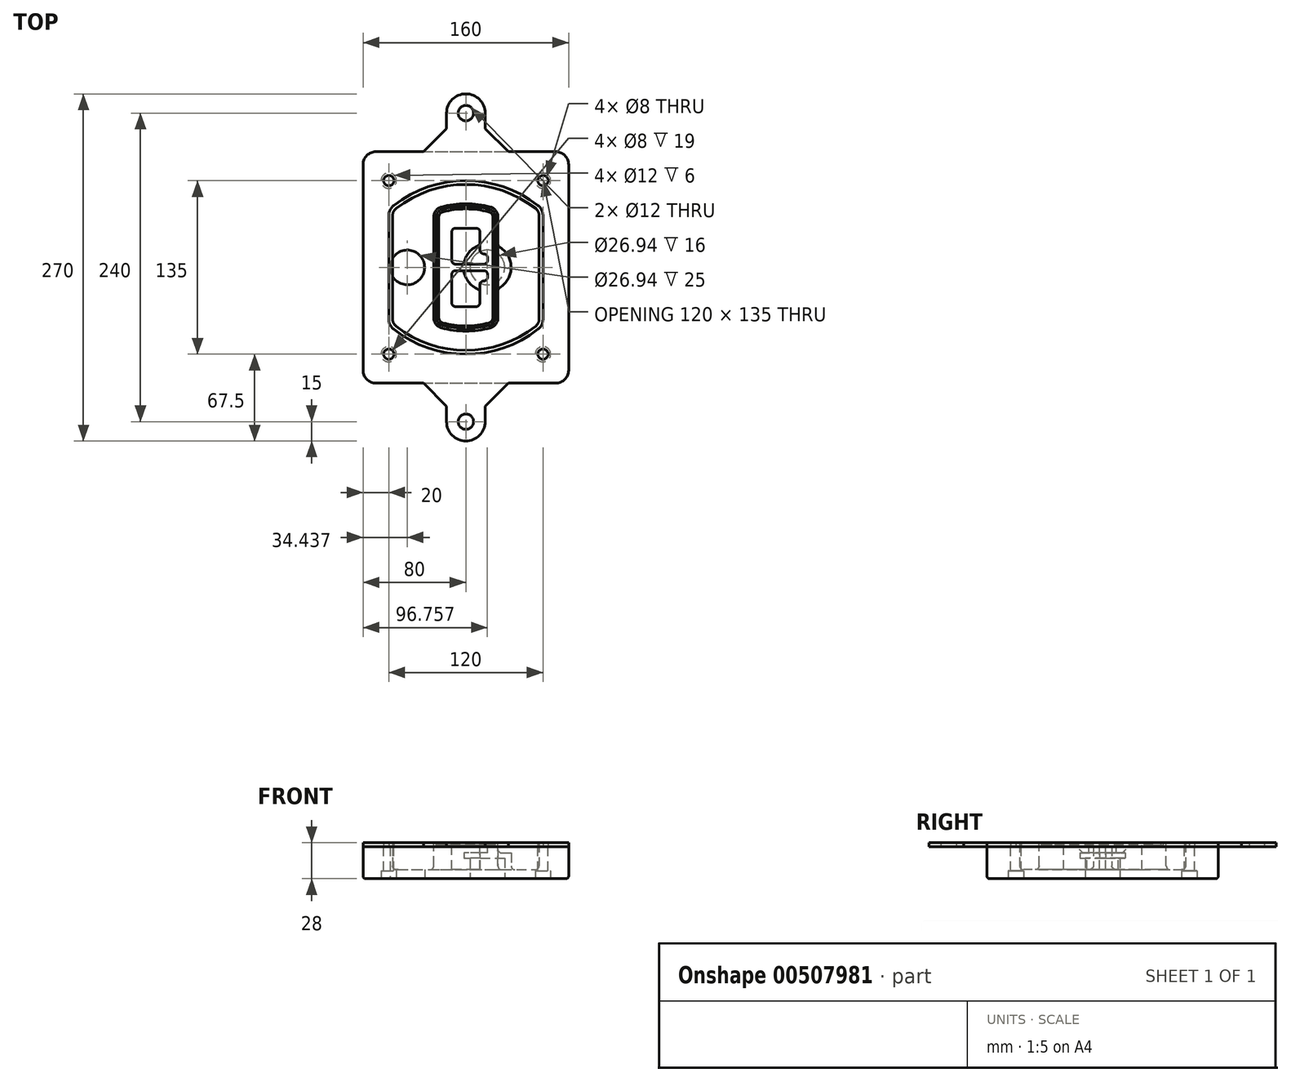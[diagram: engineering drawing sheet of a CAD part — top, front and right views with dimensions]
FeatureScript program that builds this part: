
annotation { "Feature Type Name" : "Feature", "Feature Type Description" : "" }
export const myFeature = defineFeature(function(context is Context, id is Id, definition is map)
    precondition{}
    {
        {
            var Q0;
            Q0=qCreatedBy(makeId("Top.planeOp"),FACE);
            var sketch = newSketch(context, id + "F0", { "sketchPlane" : qUnion([Q0])});
            skPoint(sketch, "E0.rect.middle", {"position": v(0, 0) * mm});
            skLineSegment(sketch, "E1.bottom", {"start": v(-70, -90) * mm, "end": v(70, -90) * mm});
            skLineSegment(sketch, "E1.top", {"start": v(-70, 90) * mm, "end": v(70, 90) * mm});
            skLineSegment(sketch, "E1.left", {"start": v(-80, -80) * mm, "end": v(-80, 80) * mm});
            skLineSegment(sketch, "E1.right", {"start": v(80, -80) * mm, "end": v(80, 80) * mm});
            skLineSegment(sketch, "E2", {"start": v(-80, 90) * mm, "end": v(80, -90) * mm, "construction": true});
            skLineSegment(sketch, "E3", {"start": v(80, 90) * mm, "end": v(-80, -90) * mm, "construction": true});
            skCircle(sketch, "E4", {"center": v(-60, 67.5) * mm, "radius": 4 * mm});
            skCircle(sketch, "E5", {"center": v(60, 67.5) * mm, "radius": 4 * mm});
            skCircle(sketch, "E6", {"center": v(60, -67.5) * mm, "radius": 4 * mm});
            skCircle(sketch, "E7", {"center": v(-60, -67.5) * mm, "radius": 4 * mm});
            skLineSegment(sketch, "E8", {"start": v(-60, 67.5) * mm, "end": v(60, 67.5) * mm, "construction": true});
            skLineSegment(sketch, "E9", {"start": v(60, 67.5) * mm, "end": v(60, -67.5) * mm, "construction": true});
            skLineSegment(sketch, "E10", {"start": v(60, -67.5) * mm, "end": v(-60, -67.5) * mm, "construction": true});
            skLineSegment(sketch, "E11", {"start": v(-60, -67.5) * mm, "end": v(-60, 67.5) * mm, "construction": true});
            skLineSegment(sketch, "E12", {"start": v(-60, 40.3) * mm, "end": v(-60, -40.3) * mm});
            skLineSegment(sketch, "E13", {"start": v(60, 40.3) * mm, "end": v(60, -40.3) * mm});
            skArc(sketch, "E14", {"start": v(56.15, 48.18) * mm, "mid": v(0, 67.5) * mm, "end": v(-56.15, 48.18) * mm});
            skArc(sketch, "E15", {"start": v(-56.15, -48.18) * mm, "mid": v(0, -67.5) * mm, "end": v(56.15, -48.18) * mm});
            skLineSegment(sketch, "E16", {"start": v(-60, 0) * mm, "end": v(60, 0) * mm, "construction": true});
            skPoint(sketch, "E17.visualSharp", {"position": v(-60, -45) * mm});
            skArc(sketch, "E17.filletArc", {"start": v(-60, -40.3) * mm, "mid": v(-58.99, -44.68) * mm, "end": v(-56.15, -48.18) * mm});
            skPoint(sketch, "E18.visualSharp", {"position": v(-60, 45) * mm});
            skArc(sketch, "E18.filletArc", {"start": v(-56.15, 48.18) * mm, "mid": v(-58.99, 44.68) * mm, "end": v(-60, 40.3) * mm});
            skPoint(sketch, "E19.visualSharp", {"position": v(60, 45) * mm});
            skArc(sketch, "E19.filletArc", {"start": v(60, 40.3) * mm, "mid": v(58.99, 44.68) * mm, "end": v(56.15, 48.18) * mm});
            skPoint(sketch, "E20.visualSharp", {"position": v(60, -45) * mm});
            skArc(sketch, "E20.filletArc", {"start": v(56.15, -48.18) * mm, "mid": v(58.99, -44.68) * mm, "end": v(60, -40.3) * mm});
            skPoint(sketch, "E21.visualSharp", {"position": v(-80, 90) * mm});
            skArc(sketch, "E21.filletArc", {"start": v(-70, 90) * mm, "mid": v(-77.07, 87.07) * mm, "end": v(-80, 80) * mm});
            skPoint(sketch, "E22.visualSharp", {"position": v(80, 90) * mm});
            skArc(sketch, "E22.filletArc", {"start": v(80, 80) * mm, "mid": v(77.07, 87.07) * mm, "end": v(70, 90) * mm});
            skPoint(sketch, "E23.visualSharp", {"position": v(80, -90) * mm});
            skArc(sketch, "E23.filletArc", {"start": v(70, -90) * mm, "mid": v(77.07, -87.07) * mm, "end": v(80, -80) * mm});
            skPoint(sketch, "E24.visualSharp", {"position": v(-80, -90) * mm});
            skArc(sketch, "E24.filletArc", {"start": v(-80, -80) * mm, "mid": v(-77.07, -87.07) * mm, "end": v(-70, -90) * mm});
            skArc(sketch, "E25.0", {"start": v(57, 40.3) * mm, "mid": v(56.3, 43.36) * mm, "end": v(54.3, 45.81) * mm});
            skLineSegment(sketch, "E25.1", {"start": v(57, 40.3) * mm, "end": v(57, -40.3) * mm});
            skArc(sketch, "E25.2", {"start": v(54.3, -45.81) * mm, "mid": v(56.3, -43.36) * mm, "end": v(57, -40.3) * mm});
            skArc(sketch, "E25.3", {"start": v(-54.3, -45.81) * mm, "mid": v(0, -64.5) * mm, "end": v(54.3, -45.81) * mm});
            skArc(sketch, "E25.4", {"start": v(-57, -40.3) * mm, "mid": v(-56.3, -43.36) * mm, "end": v(-54.3, -45.81) * mm});
            skArc(sketch, "E25.5", {"start": v(54.3, 45.81) * mm, "mid": v(0, 64.5) * mm, "end": v(-54.3, 45.81) * mm});
            skLineSegment(sketch, "E25.6", {"start": v(-57, 40.3) * mm, "end": v(-57, -40.3) * mm});
            skArc(sketch, "E25.7", {"start": v(-54.3, 45.81) * mm, "mid": v(-56.3, 43.36) * mm, "end": v(-57, 40.3) * mm});
            skArc(sketch, "E26.0", {"start": v(-58.62, 51.33) * mm, "mid": v(-62.58, 46.43) * mm, "end": v(-64, 40.3) * mm});
            skArc(sketch, "E26.1", {"start": v(58.62, 51.33) * mm, "mid": v(0, 71.5) * mm, "end": v(-58.62, 51.33) * mm});
            skArc(sketch, "E26.2", {"start": v(64, 40.3) * mm, "mid": v(62.58, 46.43) * mm, "end": v(58.62, 51.33) * mm});
            skLineSegment(sketch, "E26.3", {"start": v(64, 40.3) * mm, "end": v(64, -40.3) * mm});
            skArc(sketch, "E26.4", {"start": v(58.62, -51.33) * mm, "mid": v(62.58, -46.43) * mm, "end": v(64, -40.3) * mm});
            skLineSegment(sketch, "E26.5", {"start": v(-64, 40.3) * mm, "end": v(-64, -40.3) * mm});
            skArc(sketch, "E26.6", {"start": v(-58.62, -51.33) * mm, "mid": v(0, -71.5) * mm, "end": v(58.62, -51.33) * mm});
            skArc(sketch, "E26.7", {"start": v(-64, -40.3) * mm, "mid": v(-62.58, -46.43) * mm, "end": v(-58.62, -51.33) * mm});
            skSolve(sketch);
        }
        {
            var Q0;
            Q0=makeQuery(id+"F0.imprint","IMPRINT",FACE,{"disambiguationData":[TD([[makeQuery(id+"F0.imprint","IMPRINT",EDGE,{"derivedFrom":sQuery(id+"F0.wireOp",EDGE,"E1.bottom")}),1.0]])]});
            var Q1;
            Q1=makeQuery(id+"F0.imprint","IMPRINT",FACE,{"disambiguationData":[TD([[makeQuery(id+"F0.imprint","IMPRINT",EDGE,{"derivedFrom":sQuery(id+"F0.wireOp",EDGE,"E12")}),1.0]])]});
            var Q2;
            Q2=makeQuery(id+"F0.imprint","IMPRINT",FACE,{"disambiguationData":[TD([[makeQuery(id+"F0.imprint","IMPRINT",EDGE,{"derivedFrom":sQuery(id+"F0.wireOp",EDGE,"E25.0")}),1.0]])]});
            var Q3;
            Q3=makeQuery(id+"F0.imprint","IMPRINT",FACE,{"disambiguationData":[TD([[makeQuery(id+"F0.imprint","IMPRINT",EDGE,{"derivedFrom":sQuery(id+"F0.wireOp",EDGE,"E12")}),-1.0]])]});
            extrude(context, id + "F1", {"entities" : qUnion([Q0, Q1, Q2, Q3]), "oppositeDirection" : true, "depth" : 25 * mm});
        }
        {
            var Q0;
            Q0=makeQuery(id+"F0.imprint","IMPRINT",FACE,{"disambiguationData":[TD([[makeQuery(id+"F0.imprint","IMPRINT",EDGE,{"derivedFrom":sQuery(id+"F0.wireOp",EDGE,"E12")}),1.0]])]});
            extrude(context, id + "F2", {"entities" : qUnion([Q0]), "operationType" : NewBodyOperationType.ADD, "depth" : 3 * mm});
        }
        {
            var Q0;
            Q0=makeQuery(id+"F0.imprint","IMPRINT",FACE,{"disambiguationData":[TD([[makeQuery(id+"F0.imprint","IMPRINT",EDGE,{"derivedFrom":sQuery(id+"F0.wireOp",EDGE,"E25.0")}),1.0]])]});
            extrude(context, id + "F3", {"entities" : qUnion([Q0]), "operationType" : NewBodyOperationType.REMOVE, "oppositeDirection" : true, "depth" : 18 * mm});
        }
        {
            var Q0;
            Q0=makeQuery(id+"F2.opExtrude","CAP_FACE",FACE,{"disambiguationData":[OSD([sQuery(id+"F0.wireOp",EDGE,"E12"),sQuery(id+"F0.wireOp",EDGE,"E13"),sQuery(id+"F0.wireOp",EDGE,"E14"),sQuery(id+"F0.wireOp",EDGE,"E15"),sQuery(id+"F0.wireOp",EDGE,"E17.filletArc"),sQuery(id+"F0.wireOp",EDGE,"E18.filletArc"),sQuery(id+"F0.wireOp",EDGE,"E19.filletArc"),sQuery(id+"F0.wireOp",EDGE,"E20.filletArc"),sQuery(id+"F0.wireOp",EDGE,"E25.0"),sQuery(id+"F0.wireOp",EDGE,"E25.1"),sQuery(id+"F0.wireOp",EDGE,"E25.2"),sQuery(id+"F0.wireOp",EDGE,"E25.3"),sQuery(id+"F0.wireOp",EDGE,"E25.4"),sQuery(id+"F0.wireOp",EDGE,"E25.5"),sQuery(id+"F0.wireOp",EDGE,"E25.6"),sQuery(id+"F0.wireOp",EDGE,"E25.7")])],"isStart":false});
            var sketch = newSketch(context, id + "F4", { "sketchPlane" : qUnion([Q0])});
            skArc(sketch, "E27.0", {"start": v(-19.08, -46.97) * mm, "mid": v(0, -49.5) * mm, "end": v(19.08, -46.97) * mm});
            skArc(sketch, "E28.0", {"start": v(19.08, 46.97) * mm, "mid": v(0, 49.5) * mm, "end": v(-19.08, 46.97) * mm});
            skLineSegment(sketch, "E29", {"start": v(-25, 39.25) * mm, "end": v(-25, -39.25) * mm});
            skLineSegment(sketch, "E30", {"start": v(25, 39.25) * mm, "end": v(25, -39.25) * mm});
            skLineSegment(sketch, "E31", {"start": v(-25, 45.1) * mm, "end": v(25, 45.1) * mm, "construction": true});
            skLineSegment(sketch, "E32", {"start": v(-25, -45.1) * mm, "end": v(25, -45.1) * mm, "construction": true});
            skPoint(sketch, "E33.visualSharp", {"position": v(-25, 45.1) * mm});
            skArc(sketch, "E33.filletArc", {"start": v(-19.08, 46.97) * mm, "mid": v(-23.35, 44.11) * mm, "end": v(-25, 39.25) * mm});
            skPoint(sketch, "E34.visualSharp", {"position": v(25, 45.1) * mm});
            skArc(sketch, "E34.filletArc", {"start": v(25, 39.25) * mm, "mid": v(23.35, 44.11) * mm, "end": v(19.08, 46.97) * mm});
            skPoint(sketch, "E35.visualSharp", {"position": v(25, -45.1) * mm});
            skArc(sketch, "E35.filletArc", {"start": v(19.08, -46.97) * mm, "mid": v(23.35, -44.11) * mm, "end": v(25, -39.25) * mm});
            skPoint(sketch, "E36.visualSharp", {"position": v(-25, -45.1) * mm});
            skArc(sketch, "E36.filletArc", {"start": v(-25, -39.25) * mm, "mid": v(-23.35, -44.11) * mm, "end": v(-19.08, -46.97) * mm});
            skArc(sketch, "E37.0", {"start": v(54.3, 45.81) * mm, "mid": v(0, 64.5) * mm, "end": v(-54.3, 45.81) * mm});
            skArc(sketch, "E37.1", {"start": v(-54.3, 45.81) * mm, "mid": v(-56.3, 43.36) * mm, "end": v(-57, 40.3) * mm});
            skLineSegment(sketch, "E37.2", {"start": v(-57, 40.3) * mm, "end": v(-57, -40.3) * mm});
            skArc(sketch, "E37.3", {"start": v(-57, -40.3) * mm, "mid": v(-56.3, -43.36) * mm, "end": v(-54.3, -45.81) * mm});
            skArc(sketch, "E37.4", {"start": v(-54.3, -45.81) * mm, "mid": v(0, -64.5) * mm, "end": v(54.3, -45.81) * mm});
            skArc(sketch, "E37.5", {"start": v(54.3, -45.81) * mm, "mid": v(56.3, -43.36) * mm, "end": v(57, -40.3) * mm});
            skLineSegment(sketch, "E37.6", {"start": v(57, 40.3) * mm, "end": v(57, -40.3) * mm});
            skArc(sketch, "E37.7", {"start": v(57, 40.3) * mm, "mid": v(56.3, 43.36) * mm, "end": v(54.3, 45.81) * mm});
            skLineSegment(sketch, "E38.0", {"start": v(23, 39.25) * mm, "end": v(23, -39.25) * mm});
            skArc(sketch, "E38.1", {"start": v(18.56, -45.04) * mm, "mid": v(21.76, -42.9) * mm, "end": v(23, -39.25) * mm});
            skArc(sketch, "E38.2", {"start": v(-18.56, -45.04) * mm, "mid": v(0, -47.5) * mm, "end": v(18.56, -45.04) * mm});
            skArc(sketch, "E38.3", {"start": v(-23, -39.25) * mm, "mid": v(-21.76, -42.9) * mm, "end": v(-18.56, -45.04) * mm});
            skLineSegment(sketch, "E38.4", {"start": v(-23, 39.25) * mm, "end": v(-23, -39.25) * mm});
            skArc(sketch, "E38.5", {"start": v(23, 39.25) * mm, "mid": v(21.76, 42.9) * mm, "end": v(18.56, 45.04) * mm});
            skArc(sketch, "E38.6", {"start": v(-18.56, 45.04) * mm, "mid": v(-21.76, 42.9) * mm, "end": v(-23, 39.25) * mm});
            skArc(sketch, "E38.7", {"start": v(18.56, 45.04) * mm, "mid": v(0, 47.5) * mm, "end": v(-18.56, 45.04) * mm});
            skArc(sketch, "E39.0", {"start": v(21, 39.25) * mm, "mid": v(20.18, 41.68) * mm, "end": v(18.04, 43.1) * mm});
            skLineSegment(sketch, "E39.1", {"start": v(21, 39.25) * mm, "end": v(21, -39.25) * mm});
            skArc(sketch, "E39.2", {"start": v(18.04, -43.1) * mm, "mid": v(20.18, -41.68) * mm, "end": v(21, -39.25) * mm});
            skArc(sketch, "E39.3", {"start": v(-18.04, -43.1) * mm, "mid": v(0, -45.5) * mm, "end": v(18.04, -43.1) * mm});
            skArc(sketch, "E39.4", {"start": v(-21, -39.25) * mm, "mid": v(-20.18, -41.68) * mm, "end": v(-18.04, -43.1) * mm});
            skArc(sketch, "E39.5", {"start": v(18.04, 43.1) * mm, "mid": v(0, 45.5) * mm, "end": v(-18.04, 43.1) * mm});
            skLineSegment(sketch, "E39.6", {"start": v(-21, 39.25) * mm, "end": v(-21, -39.25) * mm});
            skArc(sketch, "E39.7", {"start": v(-18.04, 43.1) * mm, "mid": v(-20.18, 41.68) * mm, "end": v(-21, 39.25) * mm});
            skLineSegment(sketch, "E40", {"start": v(-25, 0) * mm, "end": v(25, 0) * mm, "construction": true});
            skLineSegment(sketch, "E41", {"start": v(-11, 5.5) * mm, "end": v(-11, 27.5) * mm});
            skLineSegment(sketch, "E42", {"start": v(-8, 30.5) * mm, "end": v(8, 30.5) * mm});
            skLineSegment(sketch, "E43", {"start": v(11, 27.5) * mm, "end": v(11, 13.5) * mm});
            skLineSegment(sketch, "E44", {"start": v(14, 10.5) * mm, "end": v(14, 10.5) * mm});
            skLineSegment(sketch, "E45", {"start": v(17, 7.5) * mm, "end": v(17, 5.5) * mm});
            skLineSegment(sketch, "E46", {"start": v(14, 2.5) * mm, "end": v(-8, 2.5) * mm});
            skPoint(sketch, "E47.visualSharp", {"position": v(-11, 30.5) * mm});
            skArc(sketch, "E47.filletArc", {"start": v(-8, 30.5) * mm, "mid": v(-10.12, 29.62) * mm, "end": v(-11, 27.5) * mm});
            skPoint(sketch, "E48.visualSharp", {"position": v(11, 30.5) * mm});
            skArc(sketch, "E48.filletArc", {"start": v(11, 27.5) * mm, "mid": v(10.12, 29.62) * mm, "end": v(8, 30.5) * mm});
            skPoint(sketch, "E49.visualSharp", {"position": v(11, 10.5) * mm});
            skArc(sketch, "E49.filletArc", {"start": v(11, 13.5) * mm, "mid": v(11.88, 11.38) * mm, "end": v(14, 10.5) * mm});
            skPoint(sketch, "E50.visualSharp", {"position": v(17, 10.5) * mm});
            skArc(sketch, "E50.filletArc", {"start": v(17, 7.5) * mm, "mid": v(16.12, 9.62) * mm, "end": v(14, 10.5) * mm});
            skPoint(sketch, "E51.visualSharp", {"position": v(17, 2.5) * mm});
            skArc(sketch, "E51.filletArc", {"start": v(14, 2.5) * mm, "mid": v(16.12, 3.38) * mm, "end": v(17, 5.5) * mm});
            skPoint(sketch, "E52.visualSharp", {"position": v(-11, 2.5) * mm});
            skArc(sketch, "E52.filletArc", {"start": v(-11, 5.5) * mm, "mid": v(-10.12, 3.38) * mm, "end": v(-8, 2.5) * mm});
            skLineSegment(sketch, "E53.0.MirrorCS", {"start": v(14, -2.5) * mm, "end": v(-8, -2.5) * mm});
            skArc(sketch, "E54.0.MirrorCS", {"start": v(-11, -5.5) * mm, "mid": v(-10.12, -3.38) * mm, "end": v(-8, -2.5) * mm});
            skLineSegment(sketch, "E55.0.MirrorCS", {"start": v(-11, -5.5) * mm, "end": v(-11, -27.5) * mm});
            skArc(sketch, "E56.0.MirrorCS", {"start": v(-8, -30.5) * mm, "mid": v(-10.12, -29.62) * mm, "end": v(-11, -27.5) * mm});
            skLineSegment(sketch, "E57.0.MirrorCS", {"start": v(-8, -30.5) * mm, "end": v(8, -30.5) * mm});
            skArc(sketch, "E58.0.MirrorCS", {"start": v(11, -27.5) * mm, "mid": v(10.12, -29.62) * mm, "end": v(8, -30.5) * mm});
            skLineSegment(sketch, "E59.0.MirrorCS", {"start": v(11, -27.5) * mm, "end": v(11, -13.5) * mm});
            skArc(sketch, "E60.0.MirrorCS", {"start": v(11, -13.5) * mm, "mid": v(11.88, -11.38) * mm, "end": v(14, -10.5) * mm});
            skArc(sketch, "E61.0.MirrorCS", {"start": v(17, -7.5) * mm, "mid": v(16.12, -9.62) * mm, "end": v(14, -10.5) * mm});
            skLineSegment(sketch, "E62.0.MirrorCS", {"start": v(17, -7.5) * mm, "end": v(17, -5.5) * mm});
            skArc(sketch, "E63.0.MirrorCS", {"start": v(14, -2.5) * mm, "mid": v(16.12, -3.38) * mm, "end": v(17, -5.5) * mm});
            skSolve(sketch);
        }
        {
            var Q0;
            Q0=makeQuery(id+"F4.imprint","IMPRINT",FACE,{"disambiguationData":[TD([[makeQuery(id+"F4.imprint","IMPRINT",EDGE,{"derivedFrom":sQuery(id+"F4.wireOp",EDGE,"E27.0")}),1.0]])]});
            var Q1;
            Q1=makeQuery(id+"F4.imprint","IMPRINT",FACE,{"disambiguationData":[TD([[makeQuery(id+"F4.imprint","IMPRINT",EDGE,{"derivedFrom":sQuery(id+"F4.wireOp",EDGE,"E38.0")}),-1.0]])]});
            var Q2;
            Q2=makeQuery(id+"F4.imprint","IMPRINT",FACE,{"disambiguationData":[TD([[makeQuery(id+"F4.imprint","IMPRINT",EDGE,{"derivedFrom":sQuery(id+"F4.wireOp",EDGE,"E39.0")}),1.0]])]});
            extrude(context, id + "F5", {"entities" : qUnion([Q0, Q1, Q2]), "operationType" : NewBodyOperationType.ADD, "endBound" : BoundingType.UP_TO_NEXT, "oppositeDirection" : true, "depth" : 25 * mm});
        }
        {
            var Q0;
            Q0=makeQuery(id+"F4.imprint","IMPRINT",FACE,{"disambiguationData":[TD([[makeQuery(id+"F4.imprint","IMPRINT",EDGE,{"derivedFrom":sQuery(id+"F4.wireOp",EDGE,"E38.0")}),-1.0]])]});
            extrude(context, id + "F6", {"entities" : qUnion([Q0]), "operationType" : NewBodyOperationType.REMOVE, "oppositeDirection" : true, "depth" : 2 * mm});
        }
        {
            var Q0;
            Q0=makeQuery(id+"F1.opExtrude","CAP_FACE",FACE,{"disambiguationData":[OSD([sQuery(id+"F0.wireOp",EDGE,"E1.bottom"),sQuery(id+"F0.wireOp",EDGE,"E1.top"),sQuery(id+"F0.wireOp",EDGE,"E1.left"),sQuery(id+"F0.wireOp",EDGE,"E1.right"),sQuery(id+"F0.wireOp",EDGE,"E4"),sQuery(id+"F0.wireOp",EDGE,"E5"),sQuery(id+"F0.wireOp",EDGE,"E6"),sQuery(id+"F0.wireOp",EDGE,"E7"),sQuery(id+"F0.wireOp",EDGE,"E21.filletArc"),sQuery(id+"F0.wireOp",EDGE,"E22.filletArc"),sQuery(id+"F0.wireOp",EDGE,"E23.filletArc"),sQuery(id+"F0.wireOp",EDGE,"E24.filletArc")])],"isStart":false});
            var sketch = newSketch(context, id + "F7", { "sketchPlane" : qUnion([Q0])});
            skCircle(sketch, "E64", {"center": v(16.76, 0) * mm, "radius": 13.47 * mm});
            skCircle(sketch, "E65", {"center": v(-45.56, 0) * mm, "radius": 13.47 * mm});
            skLineSegment(sketch, "E66", {"start": v(80, 0) * mm, "end": v(-80, 0) * mm});
            skCircle(sketch, "E67", {"center": v(16.76, 0) * mm, "radius": 18.47 * mm});
            skCircle(sketch, "E68", {"center": v(60, -67.5) * mm, "radius": 6 * mm});
            skCircle(sketch, "E69", {"center": v(-60, -67.5) * mm, "radius": 6 * mm});
            skCircle(sketch, "E70", {"center": v(-60, 67.5) * mm, "radius": 6 * mm});
            skCircle(sketch, "E71", {"center": v(60, 67.5) * mm, "radius": 6 * mm});
            skSolve(sketch);
        }
        {
            var Q0;
            {var subQ1=sQuery(id+"F7.wireOp",EDGE,"E66");var subQ4=sQuery(id+"F7.wireOp",EDGE,"E64");var subQ6=makeQuery(id+"F7.imprint","INTERSECT",VERTEX,{"disambiguationData":[OD(0.0)],"derivedFrom":[subQ4,subQ1]});Q0=makeQuery(id+"F7.imprint","IMPRINT",FACE,{"disambiguationData":[TD([[makeQuery(id+"F7.imprint","IMPRINT",EDGE,{"disambiguationData":[TD([[subQ6,-1.0]])],"derivedFrom":subQ4}),-1.0]])]});}
            var Q1;
            {var subQ0=sQuery(id+"F7.wireOp",EDGE,"E66");var subQ1=sQuery(id+"F7.wireOp",EDGE,"E64");var subQ3=makeQuery(id+"F7.imprint","INTERSECT",VERTEX,{"disambiguationData":[OD(0.0)],"derivedFrom":[subQ1,subQ0]});Q1=makeQuery(id+"F7.imprint","IMPRINT",FACE,{"disambiguationData":[TD([[makeQuery(id+"F7.imprint","IMPRINT",EDGE,{"disambiguationData":[TD([[subQ3,-1.0]])],"derivedFrom":subQ1}),1.0]])]});}
            var Q2;
            {var subQ0=sQuery(id+"F7.wireOp",EDGE,"E66");var subQ1=sQuery(id+"F7.wireOp",EDGE,"E64");var subQ3=makeQuery(id+"F7.imprint","INTERSECT",VERTEX,{"disambiguationData":[OD(0.0)],"derivedFrom":[subQ1,subQ0]});Q2=makeQuery(id+"F7.imprint","IMPRINT",FACE,{"disambiguationData":[TD([[makeQuery(id+"F7.imprint","IMPRINT",EDGE,{"disambiguationData":[TD([[subQ3,1.0]])],"derivedFrom":subQ1}),1.0]])]});}
            var Q3;
            {var subQ1=sQuery(id+"F7.wireOp",EDGE,"E66");var subQ4=sQuery(id+"F7.wireOp",EDGE,"E64");var subQ6=makeQuery(id+"F7.imprint","INTERSECT",VERTEX,{"disambiguationData":[OD(0.0)],"derivedFrom":[subQ4,subQ1]});Q3=makeQuery(id+"F7.imprint","IMPRINT",FACE,{"disambiguationData":[TD([[makeQuery(id+"F7.imprint","IMPRINT",EDGE,{"disambiguationData":[TD([[subQ6,1.0]])],"derivedFrom":subQ4}),-1.0]])]});}
            extrude(context, id + "F8", {"entities" : qUnion([Q0, Q1, Q2, Q3]), "operationType" : NewBodyOperationType.ADD, "oppositeDirection" : true, "depth" : 20 * mm});
        }
        {
            var Q0;
            {var subQ0=sQuery(id+"F7.wireOp",EDGE,"E66");var subQ1=sQuery(id+"F7.wireOp",EDGE,"E64");var subQ3=makeQuery(id+"F7.imprint","INTERSECT",VERTEX,{"disambiguationData":[OD(0.0)],"derivedFrom":[subQ1,subQ0]});Q0=makeQuery(id+"F7.imprint","IMPRINT",FACE,{"disambiguationData":[TD([[makeQuery(id+"F7.imprint","IMPRINT",EDGE,{"disambiguationData":[TD([[subQ3,-1.0]])],"derivedFrom":subQ1}),1.0]])]});}
            var Q1;
            {var subQ0=sQuery(id+"F7.wireOp",EDGE,"E66");var subQ1=sQuery(id+"F7.wireOp",EDGE,"E64");var subQ3=makeQuery(id+"F7.imprint","INTERSECT",VERTEX,{"disambiguationData":[OD(0.0)],"derivedFrom":[subQ1,subQ0]});Q1=makeQuery(id+"F7.imprint","IMPRINT",FACE,{"disambiguationData":[TD([[makeQuery(id+"F7.imprint","IMPRINT",EDGE,{"disambiguationData":[TD([[subQ3,1.0]])],"derivedFrom":subQ1}),1.0]])]});}
            extrude(context, id + "F9", {"entities" : qUnion([Q0, Q1]), "operationType" : NewBodyOperationType.REMOVE, "oppositeDirection" : true, "depth" : 16 * mm});
        }
        {
            var Q0;
            {var subQ0=sQuery(id+"F7.wireOp",EDGE,"E66");var subQ1=sQuery(id+"F7.wireOp",EDGE,"E65");var subQ3=makeQuery(id+"F7.imprint","INTERSECT",VERTEX,{"disambiguationData":[OD(0.0)],"derivedFrom":[subQ1,subQ0]});Q0=makeQuery(id+"F7.imprint","IMPRINT",FACE,{"disambiguationData":[TD([[makeQuery(id+"F7.imprint","IMPRINT",EDGE,{"disambiguationData":[TD([[subQ3,-1.0]])],"derivedFrom":subQ1}),1.0]])]});}
            var Q1;
            {var subQ0=sQuery(id+"F7.wireOp",EDGE,"E66");var subQ1=sQuery(id+"F7.wireOp",EDGE,"E65");var subQ3=makeQuery(id+"F7.imprint","INTERSECT",VERTEX,{"disambiguationData":[OD(0.0)],"derivedFrom":[subQ1,subQ0]});Q1=makeQuery(id+"F7.imprint","IMPRINT",FACE,{"disambiguationData":[TD([[makeQuery(id+"F7.imprint","IMPRINT",EDGE,{"disambiguationData":[TD([[subQ3,1.0]])],"derivedFrom":subQ1}),1.0]])]});}
            extrude(context, id + "F10", {"entities" : qUnion([Q0, Q1]), "operationType" : NewBodyOperationType.REMOVE, "oppositeDirection" : true, "depth" : 25 * mm});
        }
        {
            var Q0;
            Q0=makeQuery(id+"F7.imprint","IMPRINT",FACE,{"disambiguationData":[TD([[makeQuery(id+"F7.imprint","IMPRINT",EDGE,{"derivedFrom":sQuery(id+"F7.wireOp",EDGE,"E68")}),1.0]])]});
            var Q1;
            Q1=makeQuery(id+"F7.imprint","IMPRINT",FACE,{"disambiguationData":[TD([[makeQuery(id+"F7.imprint","IMPRINT",EDGE,{"derivedFrom":makeQuery(id+"F1.opExtrude","CAP_EDGE",EDGE,{"disambiguationData":[OSD([sQuery(id+"F0.wireOp",EDGE,"E5")])],"isStart":false})}),-1.0]])]});
            var Q2;
            Q2=makeQuery(id+"F7.imprint","IMPRINT",FACE,{"disambiguationData":[TD([[makeQuery(id+"F7.imprint","IMPRINT",EDGE,{"derivedFrom":sQuery(id+"F7.wireOp",EDGE,"E69")}),1.0]])]});
            var Q3;
            Q3=makeQuery(id+"F7.imprint","IMPRINT",FACE,{"disambiguationData":[TD([[makeQuery(id+"F7.imprint","IMPRINT",EDGE,{"derivedFrom":makeQuery(id+"F1.opExtrude","CAP_EDGE",EDGE,{"disambiguationData":[OSD([sQuery(id+"F0.wireOp",EDGE,"E4")])],"isStart":false})}),-1.0]])]});
            var Q4;
            Q4=makeQuery(id+"F7.imprint","IMPRINT",FACE,{"disambiguationData":[TD([[makeQuery(id+"F7.imprint","IMPRINT",EDGE,{"derivedFrom":sQuery(id+"F7.wireOp",EDGE,"E70")}),1.0]])]});
            var Q5;
            Q5=makeQuery(id+"F7.imprint","IMPRINT",FACE,{"disambiguationData":[TD([[makeQuery(id+"F7.imprint","IMPRINT",EDGE,{"derivedFrom":makeQuery(id+"F1.opExtrude","CAP_EDGE",EDGE,{"disambiguationData":[OSD([sQuery(id+"F0.wireOp",EDGE,"E7")])],"isStart":false})}),-1.0]])]});
            var Q6;
            Q6=makeQuery(id+"F7.imprint","IMPRINT",FACE,{"disambiguationData":[TD([[makeQuery(id+"F7.imprint","IMPRINT",EDGE,{"derivedFrom":sQuery(id+"F7.wireOp",EDGE,"E71")}),1.0]])]});
            var Q7;
            Q7=makeQuery(id+"F7.imprint","IMPRINT",FACE,{"disambiguationData":[TD([[makeQuery(id+"F7.imprint","IMPRINT",EDGE,{"derivedFrom":makeQuery(id+"F1.opExtrude","CAP_EDGE",EDGE,{"disambiguationData":[OSD([sQuery(id+"F0.wireOp",EDGE,"E6")])],"isStart":false})}),-1.0]])]});
            extrude(context, id + "F11", {"entities" : qUnion([Q0, Q1, Q2, Q3, Q4, Q5, Q6, Q7]), "operationType" : NewBodyOperationType.REMOVE, "oppositeDirection" : true, "depth" : 6 * mm});
        }
        {
            var Q0;
            Q0=makeQuery(id+"F9.boolean.opBoolean","COPY",FACE,{"derivedFrom":makeQuery(id+"F9.opExtrude","CAP_FACE",FACE,{"disambiguationData":[OSD([sQuery(id+"F7.wireOp",EDGE,"E64")])],"isStart":false})});
            var sketch = newSketch(context, id + "F12", { "sketchPlane" : qUnion([Q0])});
            skArc(sketch, "E72.0", {"start": v(11, 17.55) * mm, "mid": v(2.57, 11.82) * mm, "end": v(-1.54, 2.5) * mm});
            skArc(sketch, "E72.1", {"start": v(-1.54, -2.5) * mm, "mid": v(2.57, -11.82) * mm, "end": v(11, -17.55) * mm});
            skLineSegment(sketch, "E73", {"start": v(-1.54, -2.5) * mm, "end": v(14, -2.5) * mm});
            skLineSegment(sketch, "E74.0", {"start": v(14, 2.5) * mm, "end": v(-1.54, 2.5) * mm});
            skArc(sketch, "E74.1", {"start": v(14, 2.5) * mm, "mid": v(16.12, 3.38) * mm, "end": v(17, 5.5) * mm});
            skLineSegment(sketch, "E74.2", {"start": v(17, 7.5) * mm, "end": v(17, 5.5) * mm});
            skArc(sketch, "E74.3", {"start": v(17, 7.5) * mm, "mid": v(16.12, 9.62) * mm, "end": v(14, 10.5) * mm});
            skArc(sketch, "E74.4", {"start": v(11, 13.5) * mm, "mid": v(11.88, 11.38) * mm, "end": v(14, 10.5) * mm});
            skLineSegment(sketch, "E74.5", {"start": v(11, 17.55) * mm, "end": v(11, 13.5) * mm});
            skLineSegment(sketch, "E74.7", {"start": v(14, -2.5) * mm, "end": v(-1.54, -2.5) * mm});
            skArc(sketch, "E74.8", {"start": v(14, -2.5) * mm, "mid": v(16.12, -3.38) * mm, "end": v(17, -5.5) * mm});
            skLineSegment(sketch, "E74.9", {"start": v(17, -7.5) * mm, "end": v(17, -5.5) * mm});
            skArc(sketch, "E74.10", {"start": v(17, -7.5) * mm, "mid": v(16.12, -9.62) * mm, "end": v(14, -10.5) * mm});
            skArc(sketch, "E74.11", {"start": v(11, -13.5) * mm, "mid": v(11.88, -11.38) * mm, "end": v(14, -10.5) * mm});
            skLineSegment(sketch, "E74.12", {"start": v(11, -17.55) * mm, "end": v(11, -13.5) * mm});
            skPoint(sketch, "E75.orphan", {"position": v(11, -27.5) * mm});
            skPoint(sketch, "E76.orphan", {"position": v(-8, -2.5) * mm});
            skPoint(sketch, "E77.orphan", {"position": v(-8, 2.5) * mm});
            skPoint(sketch, "E78.orphan", {"position": v(11, 27.5) * mm});
            skSolve(sketch);
        }
        {
            var Q0;
            {var subQ7=sQuery(id+"F12.wireOp",EDGE,"E72.0");var subQ14=sQuery(id+"F12.wireOp",EDGE,"E72.1");var subQ16=sQuery(id+"F12.wireOp",EDGE,"E74.1");var subQ18=sQuery(id+"F12.wireOp",EDGE,"E74.8");Q0=qUnion([makeQuery(id+"F12.imprint","IMPRINT",FACE,{"disambiguationData":[TD([[makeQuery(id+"F12.imprint","IMPRINT",EDGE,{"derivedFrom":subQ7}),1.0]])]}),makeQuery(id+"F12.imprint","IMPRINT",FACE,{"disambiguationData":[TD([[makeQuery(id+"F12.imprint","IMPRINT",EDGE,{"derivedFrom":subQ14}),1.0]])]}),makeQuery(id+"F12.imprint","IMPRINT",FACE,{"disambiguationData":[TD([[makeQuery(id+"F12.imprint","IMPRINT",EDGE,{"derivedFrom":subQ16}),1.0]])]}),makeQuery(id+"F12.imprint","IMPRINT",FACE,{"disambiguationData":[TD([[makeQuery(id+"F12.imprint","IMPRINT",EDGE,{"derivedFrom":subQ18}),-1.0]])]})]);}
            var Q1;
            Q1=makeQuery(id+"F5.boolean.opBoolean","SPLIT",FACE,{"disambiguationData":[TD([makeQuery(id+"F5.opExtrude","SWEPT_FACE",FACE,{"disambiguationData":[OSD([sQuery(id+"F4.wireOp",EDGE,"E41")])]})])],"derivedFrom":makeQuery(id+"F3.boolean.opBoolean","COPY",FACE,{"derivedFrom":makeQuery(id+"F3.opExtrude","CAP_FACE",FACE,{"disambiguationData":[OSD([sQuery(id+"F0.wireOp",EDGE,"E25.0"),sQuery(id+"F0.wireOp",EDGE,"E25.1"),sQuery(id+"F0.wireOp",EDGE,"E25.2"),sQuery(id+"F0.wireOp",EDGE,"E25.3"),sQuery(id+"F0.wireOp",EDGE,"E25.4"),sQuery(id+"F0.wireOp",EDGE,"E25.5"),sQuery(id+"F0.wireOp",EDGE,"E25.6"),sQuery(id+"F0.wireOp",EDGE,"E25.7")])],"isStart":false})})});
            extrude(context, id + "F13", {"entities" : qUnion([Q0]), "operationType" : NewBodyOperationType.REMOVE, "endBound" : BoundingType.UP_TO_SURFACE, "endBoundEntityFace" : qUnion([Q1]), "depth" : 25 * mm});
        }
        {
            var Q0;
            Q0=makeQuery(id+"F3.boolean.opBoolean","COPY",EDGE,{"derivedFrom":makeQuery(id+"F3.opExtrude","CAP_EDGE",EDGE,{"disambiguationData":[OSD([sQuery(id+"F0.wireOp",EDGE,"E25.6")])],"isStart":false})});
            var Q1;
            Q1=makeQuery(id+"F8.boolean.opBoolean","INTERSECT",EDGE,{"derivedFrom":[makeQuery(id+"F5.opExtrude","SWEPT_FACE",FACE,{"disambiguationData":[OSD([sQuery(id+"F4.wireOp",EDGE,"E30")])]}),makeQuery(id+"F8.opExtrude","CAP_FACE",FACE,{"disambiguationData":[OSD([sQuery(id+"F7.wireOp",EDGE,"E67")])],"isStart":false})]});
            var Q2;
            Q2=makeQuery(id+"F8.boolean.opBoolean","INTERSECT",EDGE,{"disambiguationData":[OD(1.0)],"derivedFrom":[makeQuery(id+"F5.opExtrude","SWEPT_FACE",FACE,{"disambiguationData":[OSD([sQuery(id+"F4.wireOp",EDGE,"E30")])]}),makeQuery(id+"F8.opExtrude","SWEPT_FACE",FACE,{"disambiguationData":[OSD([sQuery(id+"F7.wireOp",EDGE,"E67")])]})]});
            var Q3;
            {var subQ0=sQuery(id+"F4.wireOp",EDGE,"E30");Q3=makeQuery(id+"F8.boolean.opBoolean","SPLIT",EDGE,{"disambiguationData":[TD([makeQuery(id+"F5.opExtrude","SWEPT_FACE",FACE,{"disambiguationData":[OSD([sQuery(id+"F4.wireOp",EDGE,"E35.filletArc")])]})])],"derivedFrom":makeQuery(id+"F5.opExtrude","CAP_EDGE",EDGE,{"disambiguationData":[OSD([subQ0])],"isStart":false})});}
            var Q4;
            {var subQ0=sQuery(id+"F0.wireOp",EDGE,"E25.7");var subQ1=sQuery(id+"F0.wireOp",EDGE,"E25.1");var subQ2=sQuery(id+"F0.wireOp",EDGE,"E25.6");var subQ3=sQuery(id+"F0.wireOp",EDGE,"E25.5");var subQ4=sQuery(id+"F0.wireOp",EDGE,"E25.4");var subQ5=sQuery(id+"F0.wireOp",EDGE,"E25.0");var subQ6=sQuery(id+"F0.wireOp",EDGE,"E25.2");var subQ7=sQuery(id+"F0.wireOp",EDGE,"E25.3");Q4=makeQuery(id+"F8.boolean.opBoolean","INTERSECT",EDGE,{"derivedFrom":[makeQuery(id+"F5.boolean.opBoolean","SPLIT",FACE,{"disambiguationData":[TD([makeQuery(id+"F2.opExtrude","SWEPT_FACE",FACE,{"disambiguationData":[OSD([subQ5])]})])],"derivedFrom":makeQuery(id+"F3.boolean.opBoolean","COPY",FACE,{"derivedFrom":makeQuery(id+"F3.opExtrude","CAP_FACE",FACE,{"disambiguationData":[OSD([subQ5,subQ1,subQ6,subQ7,subQ4,subQ3,subQ2,subQ0])],"isStart":false})})}),makeQuery(id+"F8.opExtrude","SWEPT_FACE",FACE,{"disambiguationData":[OSD([sQuery(id+"F7.wireOp",EDGE,"E67")])]})]});}
            var Q5;
            Q5=makeQuery(id+"F8.boolean.opBoolean","INTERSECT",EDGE,{"disambiguationData":[OD(0.0)],"derivedFrom":[makeQuery(id+"F5.opExtrude","SWEPT_FACE",FACE,{"disambiguationData":[OSD([sQuery(id+"F4.wireOp",EDGE,"E30")])]}),makeQuery(id+"F8.opExtrude","SWEPT_FACE",FACE,{"disambiguationData":[OSD([sQuery(id+"F7.wireOp",EDGE,"E67")])]})]});
            fillet(context, id + "F14", {"entities" : qUnion([Q0, Q1, Q2, Q3, Q4, Q5]), "radius" : 3 * mm, "tangentPropagation" : true, "allowEdgeOverflow" : false});
        }
        {
            var Q0;
            Q0=makeQuery(id+"F1.opExtrude","CAP_EDGE",EDGE,{"disambiguationData":[OSD([sQuery(id+"F0.wireOp",EDGE,"E1.bottom")])],"isStart":false});
            fillet(context, id + "F15", {"entities" : qUnion([Q0]), "radius" : 2 * mm, "tangentPropagation" : true, "allowEdgeOverflow" : false});
        }
        {
            var Q0;
            {var subQ0=sQuery(id+"F0.wireOp",EDGE,"E21.filletArc");var subQ1=sQuery(id+"F0.wireOp",EDGE,"E7");var subQ2=sQuery(id+"F0.wireOp",EDGE,"E6");var subQ3=sQuery(id+"F0.wireOp",EDGE,"E5");var subQ4=sQuery(id+"F0.wireOp",EDGE,"E4");var subQ5=sQuery(id+"F0.wireOp",EDGE,"E22.filletArc");var subQ6=sQuery(id+"F0.wireOp",EDGE,"E1.bottom");var subQ7=sQuery(id+"F0.wireOp",EDGE,"E1.right");var subQ8=sQuery(id+"F0.wireOp",EDGE,"E1.top");var subQ9=sQuery(id+"F0.wireOp",EDGE,"E1.left");var subQ10=sQuery(id+"F0.wireOp",EDGE,"E23.filletArc");var subQ11=sQuery(id+"F0.wireOp",EDGE,"E24.filletArc");Q0=makeQuery(id+"F2.boolean.opBoolean","SPLIT",FACE,{"disambiguationData":[TD([makeQuery(id+"F1.opExtrude","SWEPT_FACE",FACE,{"disambiguationData":[OSD([subQ6])]})])],"derivedFrom":makeQuery(id+"F1.opExtrude","CAP_FACE",FACE,{"disambiguationData":[OSD([subQ6,subQ8,subQ9,subQ7,subQ4,subQ3,subQ2,subQ1,subQ0,subQ5,subQ10,subQ11])],"isStart":true})});}
            var sketch = newSketch(context, id + "F16", { "sketchPlane" : qUnion([Q0])});
            skLineSegment(sketch, "E79.0", {"start": v(80, -80) * mm, "end": v(80, 80) * mm});
            skArc(sketch, "E79.1", {"start": v(70, -90) * mm, "mid": v(77.07, -87.07) * mm, "end": v(80, -80) * mm});
            skArc(sketch, "E79.2", {"start": v(80, 80) * mm, "mid": v(77.07, 87.07) * mm, "end": v(70, 90) * mm});
            skLineSegment(sketch, "E79.3", {"start": v(-70, 90) * mm, "end": v(70, 90) * mm});
            skArc(sketch, "E79.4", {"start": v(-70, 90) * mm, "mid": v(-77.07, 87.07) * mm, "end": v(-80, 80) * mm});
            skLineSegment(sketch, "E79.5", {"start": v(-80, -80) * mm, "end": v(-80, 80) * mm});
            skArc(sketch, "E79.6", {"start": v(-80, -80) * mm, "mid": v(-77.07, -87.07) * mm, "end": v(-70, -90) * mm});
            skLineSegment(sketch, "E79.7", {"start": v(-70, -90) * mm, "end": v(70, -90) * mm});
            skCircle(sketch, "E79.8", {"center": v(-60, 67.5) * mm, "radius": 4 * mm});
            skCircle(sketch, "E79.9", {"center": v(60, 67.5) * mm, "radius": 4 * mm});
            skCircle(sketch, "E79.10", {"center": v(60, -67.5) * mm, "radius": 4 * mm});
            skCircle(sketch, "E79.11", {"center": v(-60, -67.5) * mm, "radius": 4 * mm});
            skArc(sketch, "E79.12", {"start": v(56.15, 48.18) * mm, "mid": v(0, 67.5) * mm, "end": v(-56.15, 48.18) * mm});
            skLineSegment(sketch, "E79.13", {"start": v(60, 40.3) * mm, "end": v(60, -40.3) * mm});
            skArc(sketch, "E79.14", {"start": v(-56.15, -48.18) * mm, "mid": v(0, -67.5) * mm, "end": v(56.15, -48.18) * mm});
            skArc(sketch, "E79.15", {"start": v(56.15, -48.18) * mm, "mid": v(58.99, -44.68) * mm, "end": v(60, -40.3) * mm});
            skArc(sketch, "E79.16", {"start": v(-60, -40.3) * mm, "mid": v(-58.99, -44.68) * mm, "end": v(-56.15, -48.18) * mm});
            skLineSegment(sketch, "E79.17", {"start": v(-60, 40.3) * mm, "end": v(-60, -40.3) * mm});
            skArc(sketch, "E79.18", {"start": v(-56.15, 48.18) * mm, "mid": v(-58.99, 44.68) * mm, "end": v(-60, 40.3) * mm});
            skArc(sketch, "E79.19", {"start": v(60, 40.3) * mm, "mid": v(58.99, 44.68) * mm, "end": v(56.15, 48.18) * mm});
            skLineSegment(sketch, "E80", {"start": v(0, 90) * mm, "end": v(0, 120) * mm, "construction": true});
            skCircle(sketch, "E81", {"center": v(0, 120) * mm, "radius": 6 * mm});
            skLineSegment(sketch, "E82", {"start": v(-15, 108) * mm, "end": v(-15, 120) * mm});
            skLineSegment(sketch, "E83", {"start": v(15, 108) * mm, "end": v(15, 120) * mm});
            skArc(sketch, "E84", {"start": v(15, 120) * mm, "mid": v(0, 135) * mm, "end": v(-15, 120) * mm});
            skLineSegment(sketch, "E85", {"start": v(15, 108) * mm, "end": v(33, 90) * mm});
            skLineSegment(sketch, "E86", {"start": v(-15, 108) * mm, "end": v(-33, 90) * mm});
            skLineSegment(sketch, "E87", {"start": v(-80, 0) * mm, "end": v(80, 0) * mm, "construction": true});
            skArc(sketch, "E88.MirrorCS", {"start": v(15, -120) * mm, "mid": v(0, -135) * mm, "end": v(-15, -120) * mm});
            skLineSegment(sketch, "E89.MirrorCS", {"start": v(15, -108) * mm, "end": v(15, -120) * mm});
            skLineSegment(sketch, "E90.MirrorCS", {"start": v(15, -108) * mm, "end": v(33, -90) * mm});
            skLineSegment(sketch, "E91.MirrorCS", {"start": v(-15, -108) * mm, "end": v(-33, -90) * mm});
            skLineSegment(sketch, "E92.MirrorCS", {"start": v(-15, -108) * mm, "end": v(-15, -120) * mm});
            skCircle(sketch, "E93.MirrorC", {"center": v(0, -120) * mm, "radius": 6 * mm});
            skLineSegment(sketch, "E94.MirrorCS", {"start": v(0, -90) * mm, "end": v(0, -120) * mm, "construction": true});
            skSolve(sketch);
        }
        {
            var Q0;
            Q0 = qSketchRegion(id + "F16", true);
            var Q1;
            Q1=makeQuery(id+"F2.opExtrude","CAP_FACE",FACE,{"disambiguationData":[OSD([sQuery(id+"F0.wireOp",EDGE,"E12"),sQuery(id+"F0.wireOp",EDGE,"E13"),sQuery(id+"F0.wireOp",EDGE,"E14"),sQuery(id+"F0.wireOp",EDGE,"E15"),sQuery(id+"F0.wireOp",EDGE,"E17.filletArc"),sQuery(id+"F0.wireOp",EDGE,"E18.filletArc"),sQuery(id+"F0.wireOp",EDGE,"E19.filletArc"),sQuery(id+"F0.wireOp",EDGE,"E20.filletArc"),sQuery(id+"F0.wireOp",EDGE,"E25.0"),sQuery(id+"F0.wireOp",EDGE,"E25.1"),sQuery(id+"F0.wireOp",EDGE,"E25.2"),sQuery(id+"F0.wireOp",EDGE,"E25.3"),sQuery(id+"F0.wireOp",EDGE,"E25.4"),sQuery(id+"F0.wireOp",EDGE,"E25.5"),sQuery(id+"F0.wireOp",EDGE,"E25.6"),sQuery(id+"F0.wireOp",EDGE,"E25.7")])],"isStart":false});
            extrude(context, id + "F17", {"entities" : qUnion([Q0]), "endBound" : BoundingType.UP_TO_SURFACE, "endBoundEntityFace" : qUnion([Q1]), "depth" : 25 * mm});
        }
    });
